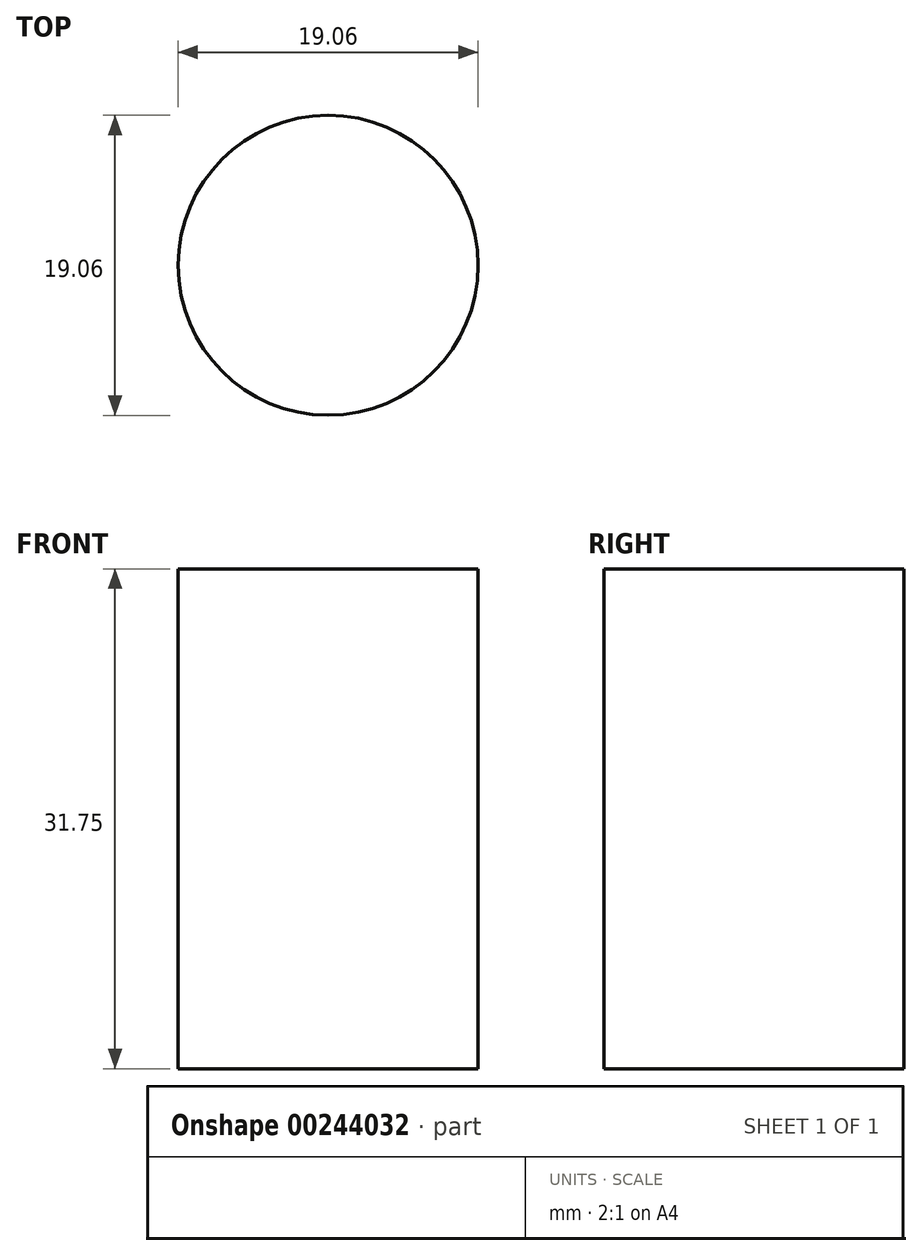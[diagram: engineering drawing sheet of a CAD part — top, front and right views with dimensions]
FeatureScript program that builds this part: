
annotation { "Feature Type Name" : "Feature", "Feature Type Description" : "" }
export const myFeature = defineFeature(function(context is Context, id is Id, definition is map)
    precondition{}
    {
        {
            var Q0;
            Q0=qCreatedBy(makeId("Top.planeOp"),FACE);
            var sketch = newSketch(context, id + "F0", { "sketchPlane" : qUnion([Q0])});
            skCircle(sketch, "E0", {"center": v(0, 0) * mm, "radius": 9.53 * mm});
            skSolve(sketch);
        }
        {
            var Q0;
            Q0 = qSketchRegion(id + "F0", true);
            extrude(context, id + "F1", {"entities" : qUnion([Q0]), "depth" : 31.75 * mm});
        }
    });
